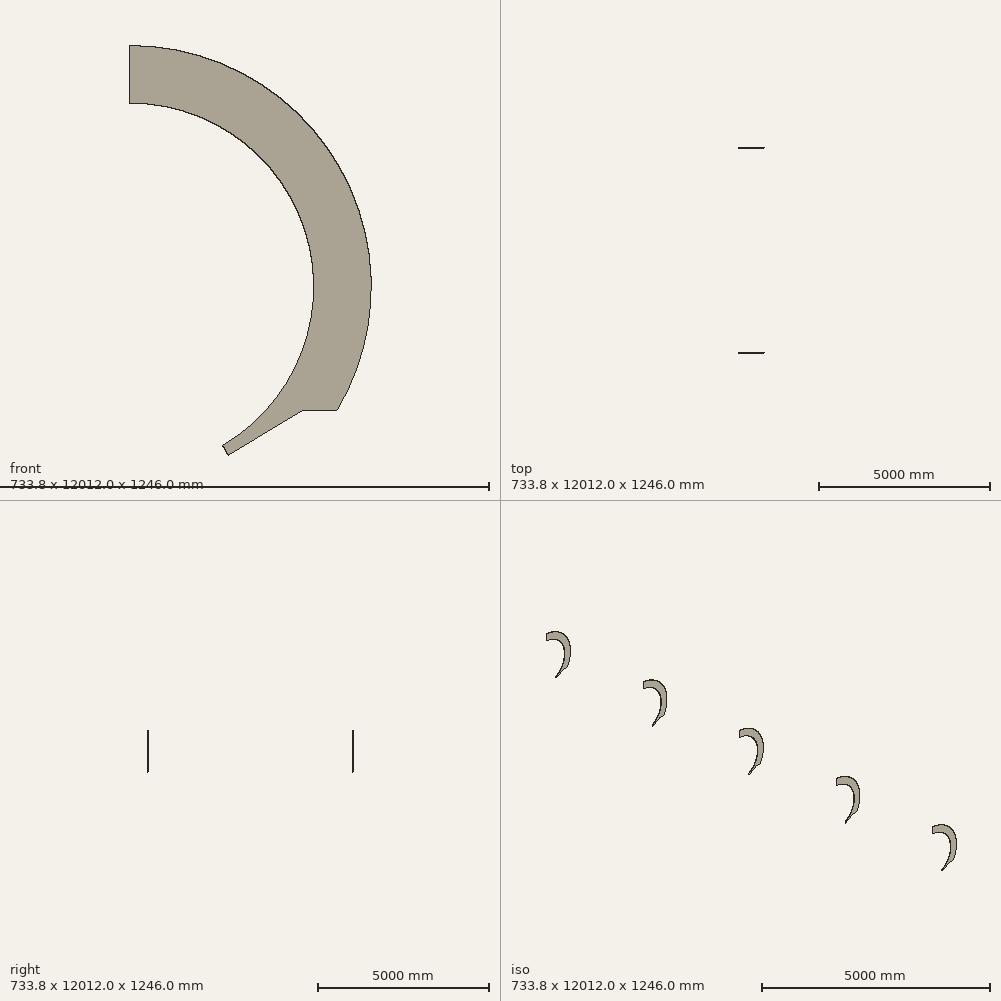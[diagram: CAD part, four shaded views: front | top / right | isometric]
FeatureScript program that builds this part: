
annotation { "Feature Type Name" : "Feature", "Feature Type Description" : "" }
export const myFeature = defineFeature(function(context is Context, id is Id, definition is map)
    precondition{}
    {
        {
            var Q0;
            Q0=qCreatedBy(makeId("Front.planeOp"),FACE);
            var sketch = newSketch(context, id + "F0", { "sketchPlane" : qUnion([Q0])});
            skCircle(sketch, "E0", {"center": v(0, 0) * mm, "radius": 733.8 * mm});
            skSolve(sketch);
        }
        {
            var Q0;
            Q0 = qSketchRegion(id + "F0", true);
            extrude(context, id + "F1", {"entities" : qUnion([Q0]), "oppositeDirection" : true, "depth" : 16050 * mm});
        }
        {
            var Q0;
            Q0=makeQuery(id+"F1.opExtrude","CAP_FACE",FACE,{"disambiguationData":[OSD([sQuery(id+"F0.wireOp",EDGE,"E0")])],"isStart":true});
            var sketch = newSketch(context, id + "F2", { "sketchPlane" : qUnion([Q0])});
            skCircle(sketch, "E1", {"center": v(0, 0) * mm, "radius": 558.8 * mm});
            skSolve(sketch);
        }
        {
            var Q0;
            Q0 = qSketchRegion(id + "F2", true);
            extrude(context, id + "F3", {"entities" : qUnion([Q0]), "operationType" : NewBodyOperationType.REMOVE, "oppositeDirection" : true, "depth" : 16050 * mm});
        }
        {
            var Q0;
            Q0=makeQuery(id+"F1.opExtrude","CAP_FACE",FACE,{"disambiguationData":[OSD([sQuery(id+"F0.wireOp",EDGE,"E0")])],"isStart":true});
            var sketch = newSketch(context, id + "F4", { "sketchPlane" : qUnion([Q0])});
            skLineSegment(sketch, "E2", {"start": v(0, 6.36) * mm, "end": v(0, -1200) * mm});
            skLineSegment(sketch, "E3", {"start": v(0, -1200) * mm, "end": v(423.06, -1200) * mm});
            skLineSegment(sketch, "E4", {"start": v(423.06, -1200) * mm, "end": v(433.06, -1217.32) * mm});
            skLineSegment(sketch, "E5", {"start": v(433.06, -1217.32) * mm, "end": v(638.14, -1098.92) * mm});
            skLineSegment(sketch, "E6", {"start": v(638.14, -1098.92) * mm, "end": v(0, 6.36) * mm});
            skSolve(sketch);
        }
        {
            var Q0;
            Q0 = qSketchRegion(id + "F4", true);
            extrude(context, id + "F5", {"entities" : qUnion([Q0]), "operationType" : NewBodyOperationType.REMOVE, "oppositeDirection" : true, "depth" : 16050 * mm});
        }
        {
            var Q0;
            Q0=qCreatedBy(makeId("Top.planeOp"),FACE);
            var sketch = newSketch(context, id + "F6", { "sketchPlane" : qUnion([Q0])});
            skLineSegment(sketch, "E7.bottom", {"start": v(0, 16050) * mm, "end": v(-6465.79, 16050) * mm});
            skLineSegment(sketch, "E7.top", {"start": v(0, 0) * mm, "end": v(-6465.79, 0) * mm});
            skLineSegment(sketch, "E7.left", {"start": v(0, 16050) * mm, "end": v(0, 0) * mm});
            skLineSegment(sketch, "E7.right", {"start": v(-6465.79, 16050) * mm, "end": v(-6465.79, 0) * mm});
            skSolve(sketch);
        }
        {
            var Q0;
            Q0 = qSketchRegion(id + "F6", true);
            extrude(context, id + "F7", {"entities" : qUnion([Q0]), "operationType" : NewBodyOperationType.REMOVE, "depth" : 3000 * mm, "hasSecondDirection" : true, "secondDirectionOppositeDirection" : true, "secondDirectionDepth" : 3000 * mm});
        }
        {
            var Q0;
            Q0=makeQuery(id+"F1.opExtrude","CAP_FACE",FACE,{"disambiguationData":[OSD([sQuery(id+"F0.wireOp",EDGE,"E0")])],"isStart":true});
            var sketch = newSketch(context, id + "F8", { "sketchPlane" : qUnion([Q0])});
            skLineSegment(sketch, "E8", {"start": v(630.03, -376.2) * mm, "end": v(524.53, -376.2) * mm});
            skLineSegment(sketch, "E9", {"start": v(524.53, -376.2) * mm, "end": v(299.4, -512.21) * mm});
            skLineSegment(sketch, "E10", {"start": v(299.4, -512.21) * mm, "end": v(369.65, -633.9) * mm});
            skArc(sketch, "E11", {"start": v(369.65, -633.9) * mm, "mid": v(516.18, -521.56) * mm, "end": v(630.03, -376.2) * mm});
            skSolve(sketch);
        }
        {
            var Q0;
            Q0 = qSketchRegion(id + "F8", true);
            extrude(context, id + "F9", {"entities" : qUnion([Q0]), "operationType" : NewBodyOperationType.REMOVE, "oppositeDirection" : true, "depth" : 16050 * mm});
        }
        {
            var Q0;
            Q0=qCreatedBy(makeId("Right.planeOp"),FACE);
            var sketch = newSketch(context, id + "F10", { "sketchPlane" : qUnion([Q0])});
            skLineSegment(sketch, "E12.bottom", {"start": v(0, 1343.66) * mm, "end": v(1518.5, 1343.66) * mm});
            skLineSegment(sketch, "E12.top", {"start": v(0, -1578.1) * mm, "end": v(1518.5, -1578.1) * mm});
            skLineSegment(sketch, "E12.left", {"start": v(0, 1343.66) * mm, "end": v(0, -1578.1) * mm});
            skLineSegment(sketch, "E12.right", {"start": v(1518.5, 1343.66) * mm, "end": v(1518.5, -1578.1) * mm});
            skLineSegment(sketch, "E13.bottom", {"start": v(1530.5, 1343.66) * mm, "end": v(4518.5, 1343.66) * mm});
            skLineSegment(sketch, "E13.top", {"start": v(1530.5, -1578.1) * mm, "end": v(4518.5, -1578.1) * mm});
            skLineSegment(sketch, "E13.left", {"start": v(1530.5, 1343.66) * mm, "end": v(1530.5, -1578.1) * mm});
            skLineSegment(sketch, "E13.right", {"start": v(4518.5, 1343.66) * mm, "end": v(4518.5, -1578.1) * mm});
            skLineSegment(sketch, "E14.bottom", {"start": v(4530.5, 1343.66) * mm, "end": v(7518.5, 1343.66) * mm});
            skLineSegment(sketch, "E14.top", {"start": v(4530.5, -1578.1) * mm, "end": v(7518.5, -1578.1) * mm});
            skLineSegment(sketch, "E14.left", {"start": v(4530.5, 1343.66) * mm, "end": v(4530.5, -1578.1) * mm});
            skLineSegment(sketch, "E14.right", {"start": v(7518.5, 1343.66) * mm, "end": v(7518.5, -1578.1) * mm});
            skLineSegment(sketch, "E15.bottom", {"start": v(7530.5, 1343.66) * mm, "end": v(10518.5, 1343.66) * mm});
            skLineSegment(sketch, "E15.top", {"start": v(7530.5, -1578.1) * mm, "end": v(10518.5, -1578.1) * mm});
            skLineSegment(sketch, "E15.left", {"start": v(7530.5, 1343.66) * mm, "end": v(7530.5, -1578.1) * mm});
            skLineSegment(sketch, "E15.right", {"start": v(10518.5, 1343.66) * mm, "end": v(10518.5, -1578.1) * mm});
            skLineSegment(sketch, "E16.bottom", {"start": v(10530.5, 1343.66) * mm, "end": v(13518.5, 1343.66) * mm});
            skLineSegment(sketch, "E16.top", {"start": v(10530.5, -1578.1) * mm, "end": v(13518.5, -1578.1) * mm});
            skLineSegment(sketch, "E16.left", {"start": v(10530.5, 1343.66) * mm, "end": v(10530.5, -1578.1) * mm});
            skLineSegment(sketch, "E16.right", {"start": v(13518.5, 1343.66) * mm, "end": v(13518.5, -1578.1) * mm});
            skLineSegment(sketch, "E17.bottom", {"start": v(13530.5, 1343.66) * mm, "end": v(16050, 1343.66) * mm});
            skLineSegment(sketch, "E17.top", {"start": v(13530.5, -1578.1) * mm, "end": v(16050, -1578.1) * mm});
            skLineSegment(sketch, "E17.left", {"start": v(13530.5, 1343.66) * mm, "end": v(13530.5, -1578.1) * mm});
            skLineSegment(sketch, "E17.right", {"start": v(16050, 1343.66) * mm, "end": v(16050, -1578.1) * mm});
            skSolve(sketch);
        }
        {
            var Q0;
            Q0 = qSketchRegion(id + "F10", true);
            extrude(context, id + "F11", {"entities" : qUnion([Q0]), "operationType" : NewBodyOperationType.REMOVE, "depth" : 3000 * mm});
        }
    });
